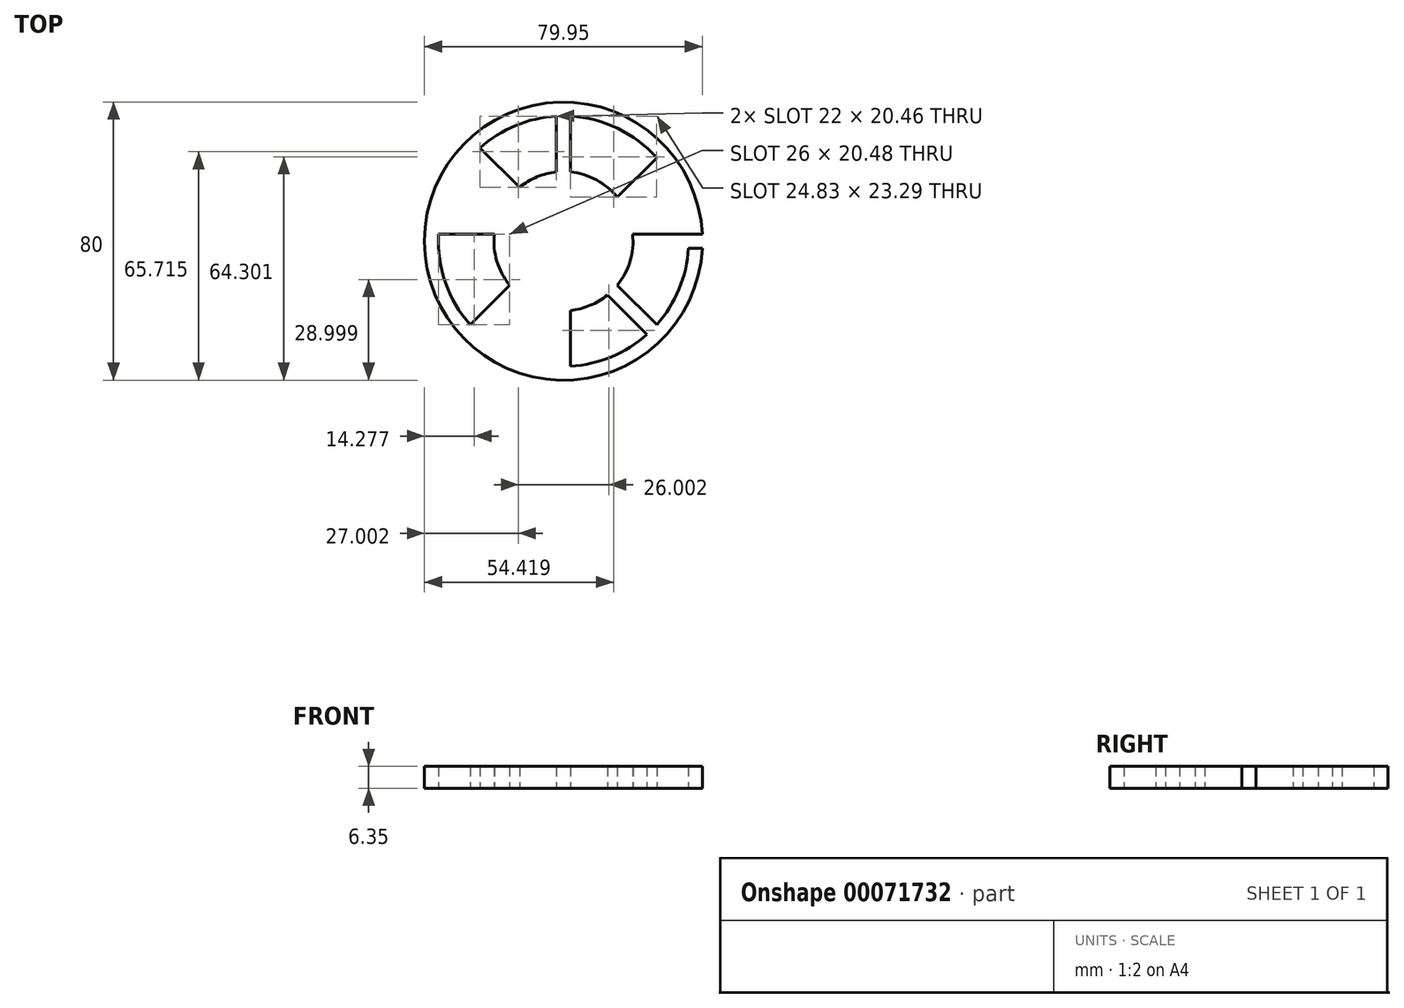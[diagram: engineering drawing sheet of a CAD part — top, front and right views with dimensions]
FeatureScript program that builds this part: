
annotation { "Feature Type Name" : "Feature", "Feature Type Description" : "" }
export const myFeature = defineFeature(function(context is Context, id is Id, definition is map)
    precondition{}
    {
        {
            var Q0;
            Q0=qCreatedBy(makeId("Top.planeOp"),FACE);
            var sketch = newSketch(context, id + "F0", { "sketchPlane" : qUnion([Q0])});
            skCircle(sketch, "E0", {"center": v(0.08, 0) * mm, "radius": 40 * mm});
            skCircle(sketch, "E1", {"center": v(0.08, 0) * mm, "radius": 36 * mm});
            skLineSegment(sketch, "E2.bottom", {"start": v(-1.92, 40) * mm, "end": v(2.08, 40) * mm});
            skLineSegment(sketch, "E2.top", {"start": v(-1.92, -40) * mm, "end": v(2.08, -40) * mm});
            skLineSegment(sketch, "E2.left", {"start": v(-1.92, 40) * mm, "end": v(-1.92, -40) * mm});
            skLineSegment(sketch, "E2.right", {"start": v(2.08, 40) * mm, "end": v(2.08, -40) * mm});
            skLineSegment(sketch, "E3", {"start": v(2.08, 0) * mm, "end": v(-1.92, 0) * mm, "construction": true});
            skPoint(sketch, "E3.endSnap0", {"position": v(-1.92, 0) * mm});
            skLineSegment(sketch, "E4.bottom", {"start": v(-39.92, -2) * mm, "end": v(40.08, -2) * mm});
            skLineSegment(sketch, "E4.top", {"start": v(-39.92, 2) * mm, "end": v(40.08, 2) * mm});
            skLineSegment(sketch, "E4.left", {"start": v(-39.92, 2) * mm, "end": v(-39.92, -2) * mm});
            skLineSegment(sketch, "E4.right", {"start": v(40.08, 2) * mm, "end": v(40.08, -2) * mm});
            skLineSegment(sketch, "E5", {"start": v(0.08, 2) * mm, "end": v(0.08, -2) * mm, "construction": true});
            skLineSegment(sketch, "E6.bottom", {"start": v(-26.79, -29.7) * mm, "end": v(29.78, 26.87) * mm});
            skLineSegment(sketch, "E6.top", {"start": v(-29.62, -26.87) * mm, "end": v(26.95, 29.7) * mm});
            skLineSegment(sketch, "E6.left", {"start": v(-29.62, -26.87) * mm, "end": v(-26.79, -29.7) * mm});
            skLineSegment(sketch, "E6.right", {"start": v(26.95, 29.7) * mm, "end": v(29.78, 26.87) * mm});
            skLineSegment(sketch, "E7", {"start": v(-1.33, 1.41) * mm, "end": v(1.5, -1.41) * mm, "construction": true});
            skLineSegment(sketch, "E8.bottom", {"start": v(-29.62, 26.87) * mm, "end": v(-26.79, 29.7) * mm});
            skLineSegment(sketch, "E8.top", {"start": v(26.95, -29.7) * mm, "end": v(29.78, -26.87) * mm});
            skLineSegment(sketch, "E8.left", {"start": v(-29.62, 26.87) * mm, "end": v(26.95, -29.7) * mm});
            skLineSegment(sketch, "E8.right", {"start": v(-26.79, 29.7) * mm, "end": v(29.78, -26.87) * mm});
            skLineSegment(sketch, "E9", {"start": v(-1.33, -1.41) * mm, "end": v(1.5, 1.41) * mm, "construction": true});
            skCircle(sketch, "E10", {"center": v(0.08, 0) * mm, "radius": 20 * mm});
            skSolve(sketch);
        }
        {
            var Q0;
            {var subQ0=sQuery(id+"F0.wireOp",EDGE,"E6.top");var subQ1=sQuery(id+"F0.wireOp",EDGE,"E0");var subQ2=makeQuery(id+"F0.imprint","INTERSECT",VERTEX,{"disambiguationData":[OD(0.0)],"derivedFrom":[subQ1,subQ0]});Q0=makeQuery(id+"F0.imprint","IMPRINT",FACE,{"disambiguationData":[TD([[makeQuery(id+"F0.imprint","IMPRINT",EDGE,{"disambiguationData":[TD([[subQ2,-1.0]])],"derivedFrom":subQ1}),1.0]])]});}
            var Q1;
            {var subQ1=sQuery(id+"F0.wireOp",EDGE,"E0");var subQ5=sQuery(id+"F0.wireOp",EDGE,"E2.right");var subQ7=makeQuery(id+"F0.imprint","INTERSECT",VERTEX,{"disambiguationData":[OD(0.0)],"derivedFrom":[subQ1,subQ5]});Q1=makeQuery(id+"F0.imprint","IMPRINT",FACE,{"disambiguationData":[TD([[makeQuery(id+"F0.imprint","IMPRINT",EDGE,{"disambiguationData":[TD([[subQ7,-1.0]])],"derivedFrom":subQ1}),1.0]])]});}
            var Q2;
            {var subQ0=sQuery(id+"F0.wireOp",EDGE,"E2.left");var subQ1=sQuery(id+"F0.wireOp",EDGE,"E0");var subQ2=makeQuery(id+"F0.imprint","INTERSECT",VERTEX,{"disambiguationData":[OD(0.0)],"derivedFrom":[subQ1,subQ0]});Q2=makeQuery(id+"F0.imprint","IMPRINT",FACE,{"disambiguationData":[TD([[makeQuery(id+"F0.imprint","IMPRINT",EDGE,{"disambiguationData":[TD([[subQ2,-1.0]])],"derivedFrom":subQ1}),1.0]])]});}
            var Q3;
            {var subQ1=sQuery(id+"F0.wireOp",EDGE,"E0");var subQ5=sQuery(id+"F0.wireOp",EDGE,"E8.right");var subQ6=makeQuery(id+"F0.imprint","INTERSECT",VERTEX,{"disambiguationData":[OD(0.0)],"derivedFrom":[subQ1,subQ5]});Q3=makeQuery(id+"F0.imprint","IMPRINT",FACE,{"disambiguationData":[TD([[makeQuery(id+"F0.imprint","IMPRINT",EDGE,{"disambiguationData":[TD([[subQ6,-1.0]])],"derivedFrom":subQ1}),1.0]])]});}
            var Q4;
            {var subQ0=sQuery(id+"F0.wireOp",EDGE,"E8.left");var subQ1=sQuery(id+"F0.wireOp",EDGE,"E0");var subQ2=makeQuery(id+"F0.imprint","INTERSECT",VERTEX,{"disambiguationData":[OD(0.0)],"derivedFrom":[subQ1,subQ0]});Q4=makeQuery(id+"F0.imprint","IMPRINT",FACE,{"disambiguationData":[TD([[makeQuery(id+"F0.imprint","IMPRINT",EDGE,{"disambiguationData":[TD([[subQ2,-1.0]])],"derivedFrom":subQ1}),1.0]])]});}
            var Q5;
            {var subQ1=sQuery(id+"F0.wireOp",EDGE,"E0");var subQ5=sQuery(id+"F0.wireOp",EDGE,"E4.top");var subQ8=makeQuery(id+"F0.imprint","INTERSECT",VERTEX,{"disambiguationData":[OD(1.0)],"derivedFrom":[subQ1,subQ5]});Q5=makeQuery(id+"F0.imprint","IMPRINT",FACE,{"disambiguationData":[TD([[makeQuery(id+"F0.imprint","IMPRINT",EDGE,{"disambiguationData":[TD([[subQ8,-1.0]])],"derivedFrom":subQ1}),1.0]])]});}
            var Q6;
            {var subQ0=sQuery(id+"F0.wireOp",EDGE,"E4.bottom");var subQ1=sQuery(id+"F0.wireOp",EDGE,"E0");var subQ2=makeQuery(id+"F0.imprint","INTERSECT",VERTEX,{"disambiguationData":[OD(0.0)],"derivedFrom":[subQ1,subQ0]});Q6=makeQuery(id+"F0.imprint","IMPRINT",FACE,{"disambiguationData":[TD([[makeQuery(id+"F0.imprint","IMPRINT",EDGE,{"disambiguationData":[TD([[subQ2,-1.0]])],"derivedFrom":subQ1}),1.0]])]});}
            var Q7;
            {var subQ1=sQuery(id+"F0.wireOp",EDGE,"E0");var subQ5=sQuery(id+"F0.wireOp",EDGE,"E6.top");var subQ6=makeQuery(id+"F0.imprint","INTERSECT",VERTEX,{"disambiguationData":[OD(1.0)],"derivedFrom":[subQ1,subQ5]});Q7=makeQuery(id+"F0.imprint","IMPRINT",FACE,{"disambiguationData":[TD([[makeQuery(id+"F0.imprint","IMPRINT",EDGE,{"disambiguationData":[TD([[subQ6,-1.0]])],"derivedFrom":subQ1}),1.0]])]});}
            var Q8;
            {var subQ0=sQuery(id+"F0.wireOp",EDGE,"E6.bottom");var subQ1=sQuery(id+"F0.wireOp",EDGE,"E0");var subQ2=makeQuery(id+"F0.imprint","INTERSECT",VERTEX,{"disambiguationData":[OD(1.0)],"derivedFrom":[subQ1,subQ0]});Q8=makeQuery(id+"F0.imprint","IMPRINT",FACE,{"disambiguationData":[TD([[makeQuery(id+"F0.imprint","IMPRINT",EDGE,{"disambiguationData":[TD([[subQ2,-1.0]])],"derivedFrom":subQ1}),1.0]])]});}
            var Q9;
            {var subQ0=sQuery(id+"F0.wireOp",EDGE,"E2.left");var subQ5=sQuery(id+"F0.wireOp",EDGE,"E0");var subQ6=makeQuery(id+"F0.imprint","INTERSECT",VERTEX,{"disambiguationData":[OD(1.0)],"derivedFrom":[subQ5,subQ0]});Q9=makeQuery(id+"F0.imprint","IMPRINT",FACE,{"disambiguationData":[TD([[makeQuery(id+"F0.imprint","IMPRINT",EDGE,{"disambiguationData":[TD([[subQ6,-1.0]])],"derivedFrom":subQ5}),1.0]])]});}
            var Q10;
            {var subQ0=sQuery(id+"F0.wireOp",EDGE,"E2.right");var subQ1=sQuery(id+"F0.wireOp",EDGE,"E0");var subQ2=makeQuery(id+"F0.imprint","INTERSECT",VERTEX,{"disambiguationData":[OD(1.0)],"derivedFrom":[subQ1,subQ0]});Q10=makeQuery(id+"F0.imprint","IMPRINT",FACE,{"disambiguationData":[TD([[makeQuery(id+"F0.imprint","IMPRINT",EDGE,{"disambiguationData":[TD([[subQ2,-1.0]])],"derivedFrom":subQ1}),1.0]])]});}
            var Q11;
            {var subQ0=sQuery(id+"F0.wireOp",EDGE,"E8.left");var subQ1=sQuery(id+"F0.wireOp",EDGE,"E0");var subQ2=makeQuery(id+"F0.imprint","INTERSECT",VERTEX,{"disambiguationData":[OD(1.0)],"derivedFrom":[subQ1,subQ0]});Q11=makeQuery(id+"F0.imprint","IMPRINT",FACE,{"disambiguationData":[TD([[makeQuery(id+"F0.imprint","IMPRINT",EDGE,{"disambiguationData":[TD([[subQ2,-1.0]])],"derivedFrom":subQ1}),1.0]])]});}
            var Q12;
            {var subQ0=sQuery(id+"F0.wireOp",EDGE,"E8.right");var subQ1=sQuery(id+"F0.wireOp",EDGE,"E0");var subQ2=makeQuery(id+"F0.imprint","INTERSECT",VERTEX,{"disambiguationData":[OD(1.0)],"derivedFrom":[subQ1,subQ0]});Q12=makeQuery(id+"F0.imprint","IMPRINT",FACE,{"disambiguationData":[TD([[makeQuery(id+"F0.imprint","IMPRINT",EDGE,{"disambiguationData":[TD([[subQ2,-1.0]])],"derivedFrom":subQ1}),1.0]])]});}
            var Q13;
            {var subQ1=sQuery(id+"F0.wireOp",EDGE,"E0");var subQ5=sQuery(id+"F0.wireOp",EDGE,"E4.top");var subQ7=makeQuery(id+"F0.imprint","INTERSECT",VERTEX,{"disambiguationData":[OD(0.0)],"derivedFrom":[subQ1,subQ5]});Q13=makeQuery(id+"F0.imprint","IMPRINT",FACE,{"disambiguationData":[TD([[makeQuery(id+"F0.imprint","IMPRINT",EDGE,{"disambiguationData":[TD([[subQ7,1.0]])],"derivedFrom":subQ1}),1.0]])]});}
            var Q14;
            {var subQ0=sQuery(id+"F0.wireOp",EDGE,"E4.top");var subQ1=sQuery(id+"F0.wireOp",EDGE,"E0");var subQ2=makeQuery(id+"F0.imprint","INTERSECT",VERTEX,{"disambiguationData":[OD(0.0)],"derivedFrom":[subQ1,subQ0]});Q14=makeQuery(id+"F0.imprint","IMPRINT",FACE,{"disambiguationData":[TD([[makeQuery(id+"F0.imprint","IMPRINT",EDGE,{"disambiguationData":[TD([[subQ2,-1.0]])],"derivedFrom":subQ1}),1.0]])]});}
            var Q15;
            {var subQ0=sQuery(id+"F0.wireOp",EDGE,"E6.bottom");var subQ1=sQuery(id+"F0.wireOp",EDGE,"E0");var subQ2=makeQuery(id+"F0.imprint","INTERSECT",VERTEX,{"disambiguationData":[OD(0.0)],"derivedFrom":[subQ1,subQ0]});Q15=makeQuery(id+"F0.imprint","IMPRINT",FACE,{"disambiguationData":[TD([[makeQuery(id+"F0.imprint","IMPRINT",EDGE,{"disambiguationData":[TD([[subQ2,-1.0]])],"derivedFrom":subQ1}),1.0]])]});}
            var Q16;
            {var subQ0=sQuery(id+"F0.wireOp",EDGE,"E6.bottom");var subQ1=sQuery(id+"F0.wireOp",EDGE,"E1");var subQ2=makeQuery(id+"F0.imprint","INTERSECT",VERTEX,{"disambiguationData":[OD(0.0)],"derivedFrom":[subQ1,subQ0]});Q16=makeQuery(id+"F0.imprint","IMPRINT",FACE,{"disambiguationData":[TD([[makeQuery(id+"F0.imprint","IMPRINT",EDGE,{"disambiguationData":[TD([[subQ2,-1.0]])],"derivedFrom":subQ1}),1.0]])]});}
            var Q17;
            {var subQ0=sQuery(id+"F0.wireOp",EDGE,"E4.top");var subQ1=sQuery(id+"F0.wireOp",EDGE,"E1");var subQ2=makeQuery(id+"F0.imprint","INTERSECT",VERTEX,{"disambiguationData":[OD(0.0)],"derivedFrom":[subQ1,subQ0]});Q17=makeQuery(id+"F0.imprint","IMPRINT",FACE,{"disambiguationData":[TD([[makeQuery(id+"F0.imprint","IMPRINT",EDGE,{"disambiguationData":[TD([[subQ2,1.0]])],"derivedFrom":subQ1}),1.0]])]});}
            var Q18;
            {var subQ0=sQuery(id+"F0.wireOp",EDGE,"E8.left");var subQ1=sQuery(id+"F0.wireOp",EDGE,"E1");var subQ2=makeQuery(id+"F0.imprint","INTERSECT",VERTEX,{"disambiguationData":[OD(1.0)],"derivedFrom":[subQ1,subQ0]});Q18=makeQuery(id+"F0.imprint","IMPRINT",FACE,{"disambiguationData":[TD([[makeQuery(id+"F0.imprint","IMPRINT",EDGE,{"disambiguationData":[TD([[subQ2,-1.0]])],"derivedFrom":subQ1}),1.0]])]});}
            var Q19;
            {var subQ0=sQuery(id+"F0.wireOp",EDGE,"E2.left");var subQ1=sQuery(id+"F0.wireOp",EDGE,"E1");var subQ2=makeQuery(id+"F0.imprint","INTERSECT",VERTEX,{"disambiguationData":[OD(1.0)],"derivedFrom":[subQ1,subQ0]});Q19=makeQuery(id+"F0.imprint","IMPRINT",FACE,{"disambiguationData":[TD([[makeQuery(id+"F0.imprint","IMPRINT",EDGE,{"disambiguationData":[TD([[subQ2,-1.0]])],"derivedFrom":subQ1}),1.0]])]});}
            var Q20;
            {var subQ0=sQuery(id+"F0.wireOp",EDGE,"E6.top");var subQ1=sQuery(id+"F0.wireOp",EDGE,"E1");var subQ2=makeQuery(id+"F0.imprint","INTERSECT",VERTEX,{"disambiguationData":[OD(1.0)],"derivedFrom":[subQ1,subQ0]});Q20=makeQuery(id+"F0.imprint","IMPRINT",FACE,{"disambiguationData":[TD([[makeQuery(id+"F0.imprint","IMPRINT",EDGE,{"disambiguationData":[TD([[subQ2,-1.0]])],"derivedFrom":subQ1}),1.0]])]});}
            var Q21;
            {var subQ0=sQuery(id+"F0.wireOp",EDGE,"E4.top");var subQ1=sQuery(id+"F0.wireOp",EDGE,"E1");var subQ2=makeQuery(id+"F0.imprint","INTERSECT",VERTEX,{"disambiguationData":[OD(1.0)],"derivedFrom":[subQ1,subQ0]});Q21=makeQuery(id+"F0.imprint","IMPRINT",FACE,{"disambiguationData":[TD([[makeQuery(id+"F0.imprint","IMPRINT",EDGE,{"disambiguationData":[TD([[subQ2,-1.0]])],"derivedFrom":subQ1}),1.0]])]});}
            var Q22;
            {var subQ0=sQuery(id+"F0.wireOp",EDGE,"E8.right");var subQ1=sQuery(id+"F0.wireOp",EDGE,"E1");var subQ2=makeQuery(id+"F0.imprint","INTERSECT",VERTEX,{"disambiguationData":[OD(0.0)],"derivedFrom":[subQ1,subQ0]});Q22=makeQuery(id+"F0.imprint","IMPRINT",FACE,{"disambiguationData":[TD([[makeQuery(id+"F0.imprint","IMPRINT",EDGE,{"disambiguationData":[TD([[subQ2,-1.0]])],"derivedFrom":subQ1}),1.0]])]});}
            var Q23;
            {var subQ0=sQuery(id+"F0.wireOp",EDGE,"E2.right");var subQ1=sQuery(id+"F0.wireOp",EDGE,"E1");var subQ2=makeQuery(id+"F0.imprint","INTERSECT",VERTEX,{"disambiguationData":[OD(0.0)],"derivedFrom":[subQ1,subQ0]});Q23=makeQuery(id+"F0.imprint","IMPRINT",FACE,{"disambiguationData":[TD([[makeQuery(id+"F0.imprint","IMPRINT",EDGE,{"disambiguationData":[TD([[subQ2,-1.0]])],"derivedFrom":subQ1}),1.0]])]});}
            var Q24;
            {var subQ1=sQuery(id+"F0.wireOp",EDGE,"E2.left");var subQ5=sQuery(id+"F0.wireOp",EDGE,"E10");var subQ9=makeQuery(id+"F0.imprint","INTERSECT",VERTEX,{"disambiguationData":[OD(0.0)],"derivedFrom":[subQ1,subQ5]});Q24=makeQuery(id+"F0.imprint","IMPRINT",FACE,{"disambiguationData":[TD([[makeQuery(id+"F0.imprint","IMPRINT",EDGE,{"disambiguationData":[TD([[subQ9,-1.0]])],"derivedFrom":subQ1}),1.0]])]});}
            var Q25;
            {var subQ0=sQuery(id+"F0.wireOp",EDGE,"E10");var subQ1=sQuery(id+"F0.wireOp",EDGE,"E2.right");var subQ2=makeQuery(id+"F0.imprint","INTERSECT",VERTEX,{"disambiguationData":[OD(0.0)],"derivedFrom":[subQ1,subQ0]});Q25=makeQuery(id+"F0.imprint","IMPRINT",FACE,{"disambiguationData":[TD([[makeQuery(id+"F0.imprint","IMPRINT",EDGE,{"disambiguationData":[TD([[subQ2,-1.0]])],"derivedFrom":subQ1}),1.0]])]});}
            var Q26;
            {var subQ0=sQuery(id+"F0.wireOp",EDGE,"E6.top");var subQ1=sQuery(id+"F0.wireOp",EDGE,"E2.right");var subQ2=makeQuery(id+"F0.imprint","INTERSECT",VERTEX,{"derivedFrom":[subQ1,subQ0]});Q26=makeQuery(id+"F0.imprint","IMPRINT",FACE,{"disambiguationData":[TD([[makeQuery(id+"F0.imprint","IMPRINT",EDGE,{"disambiguationData":[TD([[subQ2,-1.0]])],"derivedFrom":subQ1}),1.0]])]});}
            var Q27;
            {var subQ0=sQuery(id+"F0.wireOp",EDGE,"E8.right");var subQ1=sQuery(id+"F0.wireOp",EDGE,"E4.bottom");var subQ2=makeQuery(id+"F0.imprint","INTERSECT",VERTEX,{"derivedFrom":[subQ1,subQ0]});Q27=makeQuery(id+"F0.imprint","IMPRINT",FACE,{"disambiguationData":[TD([[makeQuery(id+"F0.imprint","IMPRINT",EDGE,{"disambiguationData":[TD([[subQ2,-1.0]])],"derivedFrom":subQ1}),1.0]])]});}
            var Q28;
            {var subQ0=sQuery(id+"F0.wireOp",EDGE,"E6.bottom");var subQ1=sQuery(id+"F0.wireOp",EDGE,"E4.top");var subQ2=makeQuery(id+"F0.imprint","INTERSECT",VERTEX,{"derivedFrom":[subQ1,subQ0]});Q28=makeQuery(id+"F0.imprint","IMPRINT",FACE,{"disambiguationData":[TD([[makeQuery(id+"F0.imprint","IMPRINT",EDGE,{"disambiguationData":[TD([[subQ2,-1.0]])],"derivedFrom":subQ1}),1.0]])]});}
            var Q29;
            {var subQ0=sQuery(id+"F0.wireOp",EDGE,"E8.right");var subQ1=sQuery(id+"F0.wireOp",EDGE,"E4.bottom");var subQ2=makeQuery(id+"F0.imprint","INTERSECT",VERTEX,{"derivedFrom":[subQ1,subQ0]});Q29=makeQuery(id+"F0.imprint","IMPRINT",FACE,{"disambiguationData":[TD([[makeQuery(id+"F0.imprint","IMPRINT",EDGE,{"disambiguationData":[TD([[subQ2,-1.0]])],"derivedFrom":subQ1}),-1.0]])]});}
            var Q30;
            {var subQ1=sQuery(id+"F0.wireOp",EDGE,"E4.bottom");var subQ6=sQuery(id+"F0.wireOp",EDGE,"E2.right");var subQ9=makeQuery(id+"F0.imprint","INTERSECT",VERTEX,{"derivedFrom":[subQ6,subQ1]});Q30=makeQuery(id+"F0.imprint","IMPRINT",FACE,{"disambiguationData":[TD([[makeQuery(id+"F0.imprint","IMPRINT",EDGE,{"disambiguationData":[TD([[subQ9,-1.0]])],"derivedFrom":subQ6}),1.0]])]});}
            var Q31;
            {var subQ0=sQuery(id+"F0.wireOp",EDGE,"E8.left");var subQ1=sQuery(id+"F0.wireOp",EDGE,"E2.right");var subQ2=makeQuery(id+"F0.imprint","INTERSECT",VERTEX,{"derivedFrom":[subQ1,subQ0]});Q31=makeQuery(id+"F0.imprint","IMPRINT",FACE,{"disambiguationData":[TD([[makeQuery(id+"F0.imprint","IMPRINT",EDGE,{"disambiguationData":[TD([[subQ2,-1.0]])],"derivedFrom":subQ1}),1.0]])]});}
            var Q32;
            {var subQ3=sQuery(id+"F0.wireOp",EDGE,"E6.bottom");var subQ5=sQuery(id+"F0.wireOp",EDGE,"E2.left");var subQ6=makeQuery(id+"F0.imprint","INTERSECT",VERTEX,{"derivedFrom":[subQ5,subQ3]});Q32=makeQuery(id+"F0.imprint","IMPRINT",FACE,{"disambiguationData":[TD([[makeQuery(id+"F0.imprint","IMPRINT",EDGE,{"disambiguationData":[TD([[subQ6,-1.0]])],"derivedFrom":subQ5}),1.0]])]});}
            var Q33;
            {var subQ0=sQuery(id+"F0.wireOp",EDGE,"E6.bottom");var subQ1=sQuery(id+"F0.wireOp",EDGE,"E2.left");var subQ2=makeQuery(id+"F0.imprint","INTERSECT",VERTEX,{"derivedFrom":[subQ1,subQ0]});Q33=makeQuery(id+"F0.imprint","IMPRINT",FACE,{"disambiguationData":[TD([[makeQuery(id+"F0.imprint","IMPRINT",EDGE,{"disambiguationData":[TD([[subQ2,-1.0]])],"derivedFrom":subQ1}),-1.0]])]});}
            var Q34;
            {var subQ1=sQuery(id+"F0.wireOp",EDGE,"E4.bottom");var subQ5=sQuery(id+"F0.wireOp",EDGE,"E2.left");var subQ6=makeQuery(id+"F0.imprint","INTERSECT",VERTEX,{"derivedFrom":[subQ5,subQ1]});Q34=makeQuery(id+"F0.imprint","IMPRINT",FACE,{"disambiguationData":[TD([[makeQuery(id+"F0.imprint","IMPRINT",EDGE,{"disambiguationData":[TD([[subQ6,-1.0]])],"derivedFrom":subQ5}),-1.0]])]});}
            var Q35;
            {var subQ0=sQuery(id+"F0.wireOp",EDGE,"E10");var subQ1=sQuery(id+"F0.wireOp",EDGE,"E4.bottom");var subQ2=makeQuery(id+"F0.imprint","INTERSECT",VERTEX,{"disambiguationData":[OD(0.0)],"derivedFrom":[subQ1,subQ0]});Q35=makeQuery(id+"F0.imprint","IMPRINT",FACE,{"disambiguationData":[TD([[makeQuery(id+"F0.imprint","IMPRINT",EDGE,{"disambiguationData":[TD([[subQ2,-1.0]])],"derivedFrom":subQ1}),-1.0]])]});}
            var Q36;
            {var subQ5=sQuery(id+"F0.wireOp",EDGE,"E4.bottom");var subQ7=sQuery(id+"F0.wireOp",EDGE,"E10");var subQ9=makeQuery(id+"F0.imprint","INTERSECT",VERTEX,{"disambiguationData":[OD(0.0)],"derivedFrom":[subQ5,subQ7]});Q36=makeQuery(id+"F0.imprint","IMPRINT",FACE,{"disambiguationData":[TD([[makeQuery(id+"F0.imprint","IMPRINT",EDGE,{"disambiguationData":[TD([[subQ9,-1.0]])],"derivedFrom":subQ5}),1.0]])]});}
            var Q37;
            {var subQ0=sQuery(id+"F0.wireOp",EDGE,"E10");var subQ1=sQuery(id+"F0.wireOp",EDGE,"E4.top");var subQ2=makeQuery(id+"F0.imprint","INTERSECT",VERTEX,{"disambiguationData":[OD(0.0)],"derivedFrom":[subQ1,subQ0]});Q37=makeQuery(id+"F0.imprint","IMPRINT",FACE,{"disambiguationData":[TD([[makeQuery(id+"F0.imprint","IMPRINT",EDGE,{"disambiguationData":[TD([[subQ2,-1.0]])],"derivedFrom":subQ1}),1.0]])]});}
            var Q38;
            {var subQ5=sQuery(id+"F0.wireOp",EDGE,"E8.right");var subQ6=sQuery(id+"F0.wireOp",EDGE,"E2.left");var subQ7=makeQuery(id+"F0.imprint","INTERSECT",VERTEX,{"derivedFrom":[subQ6,subQ5]});Q38=makeQuery(id+"F0.imprint","IMPRINT",FACE,{"disambiguationData":[TD([[makeQuery(id+"F0.imprint","IMPRINT",EDGE,{"disambiguationData":[TD([[subQ7,-1.0]])],"derivedFrom":subQ6}),-1.0]])]});}
            var Q39;
            {var subQ0=sQuery(id+"F0.wireOp",EDGE,"E10");var subQ1=sQuery(id+"F0.wireOp",EDGE,"E2.left");var subQ2=makeQuery(id+"F0.imprint","INTERSECT",VERTEX,{"disambiguationData":[OD(0.0)],"derivedFrom":[subQ1,subQ0]});Q39=makeQuery(id+"F0.imprint","IMPRINT",FACE,{"disambiguationData":[TD([[makeQuery(id+"F0.imprint","IMPRINT",EDGE,{"disambiguationData":[TD([[subQ2,-1.0]])],"derivedFrom":subQ1}),-1.0]])]});}
            var Q40;
            {var subQ0=sQuery(id+"F0.wireOp",EDGE,"E4.top");var subQ1=sQuery(id+"F0.wireOp",EDGE,"E2.right");var subQ2=makeQuery(id+"F0.imprint","INTERSECT",VERTEX,{"derivedFrom":[subQ1,subQ0]});Q40=makeQuery(id+"F0.imprint","IMPRINT",FACE,{"disambiguationData":[TD([[makeQuery(id+"F0.imprint","IMPRINT",EDGE,{"disambiguationData":[TD([[subQ2,-1.0]])],"derivedFrom":subQ1}),1.0]])]});}
            var Q41;
            {var subQ0=sQuery(id+"F0.wireOp",EDGE,"E6.bottom");var subQ1=sQuery(id+"F0.wireOp",EDGE,"E2.right");var subQ2=makeQuery(id+"F0.imprint","INTERSECT",VERTEX,{"derivedFrom":[subQ1,subQ0]});Q41=makeQuery(id+"F0.imprint","IMPRINT",FACE,{"disambiguationData":[TD([[makeQuery(id+"F0.imprint","IMPRINT",EDGE,{"disambiguationData":[TD([[subQ2,-1.0]])],"derivedFrom":subQ1}),1.0]])]});}
            var Q42;
            {var subQ0=sQuery(id+"F0.wireOp",EDGE,"E4.bottom");var subQ1=sQuery(id+"F0.wireOp",EDGE,"E2.right");var subQ2=makeQuery(id+"F0.imprint","INTERSECT",VERTEX,{"derivedFrom":[subQ1,subQ0]});Q42=makeQuery(id+"F0.imprint","IMPRINT",FACE,{"disambiguationData":[TD([[makeQuery(id+"F0.imprint","IMPRINT",EDGE,{"disambiguationData":[TD([[subQ2,-1.0]])],"derivedFrom":subQ1}),-1.0]])]});}
            var Q43;
            {var subQ0=sQuery(id+"F0.wireOp",EDGE,"E4.bottom");var subQ1=sQuery(id+"F0.wireOp",EDGE,"E2.left");var subQ2=makeQuery(id+"F0.imprint","INTERSECT",VERTEX,{"derivedFrom":[subQ1,subQ0]});Q43=makeQuery(id+"F0.imprint","IMPRINT",FACE,{"disambiguationData":[TD([[makeQuery(id+"F0.imprint","IMPRINT",EDGE,{"disambiguationData":[TD([[subQ2,-1.0]])],"derivedFrom":subQ1}),1.0]])]});}
            var Q44;
            {var subQ0=sQuery(id+"F0.wireOp",EDGE,"E4.top");var subQ1=sQuery(id+"F0.wireOp",EDGE,"E2.left");var subQ2=makeQuery(id+"F0.imprint","INTERSECT",VERTEX,{"derivedFrom":[subQ1,subQ0]});Q44=makeQuery(id+"F0.imprint","IMPRINT",FACE,{"disambiguationData":[TD([[makeQuery(id+"F0.imprint","IMPRINT",EDGE,{"disambiguationData":[TD([[subQ2,-1.0]])],"derivedFrom":subQ1}),-1.0]])]});}
            var Q45;
            {var subQ0=sQuery(id+"F0.wireOp",EDGE,"E6.top");var subQ1=sQuery(id+"F0.wireOp",EDGE,"E2.right");var subQ2=makeQuery(id+"F0.imprint","INTERSECT",VERTEX,{"derivedFrom":[subQ1,subQ0]});Q45=makeQuery(id+"F0.imprint","IMPRINT",FACE,{"disambiguationData":[TD([[makeQuery(id+"F0.imprint","IMPRINT",EDGE,{"disambiguationData":[TD([[subQ2,-1.0]])],"derivedFrom":subQ1}),-1.0]])]});}
            var Q46;
            {var subQ0=sQuery(id+"F0.wireOp",EDGE,"E8.right");var subQ1=sQuery(id+"F0.wireOp",EDGE,"E2.right");var subQ2=makeQuery(id+"F0.imprint","INTERSECT",VERTEX,{"derivedFrom":[subQ1,subQ0]});Q46=makeQuery(id+"F0.imprint","IMPRINT",FACE,{"disambiguationData":[TD([[makeQuery(id+"F0.imprint","IMPRINT",EDGE,{"disambiguationData":[TD([[subQ2,-1.0]])],"derivedFrom":subQ1}),1.0]])]});}
            var Q47;
            {var subQ0=sQuery(id+"F0.wireOp",EDGE,"E6.bottom");var subQ1=sQuery(id+"F0.wireOp",EDGE,"E2.right");var subQ2=makeQuery(id+"F0.imprint","INTERSECT",VERTEX,{"derivedFrom":[subQ1,subQ0]});Q47=makeQuery(id+"F0.imprint","IMPRINT",FACE,{"disambiguationData":[TD([[makeQuery(id+"F0.imprint","IMPRINT",EDGE,{"disambiguationData":[TD([[subQ2,-1.0]])],"derivedFrom":subQ1}),-1.0]])]});}
            var Q48;
            {var subQ0=sQuery(id+"F0.wireOp",EDGE,"E8.left");var subQ1=sQuery(id+"F0.wireOp",EDGE,"E4.bottom");var subQ2=makeQuery(id+"F0.imprint","INTERSECT",VERTEX,{"derivedFrom":[subQ1,subQ0]});Q48=makeQuery(id+"F0.imprint","IMPRINT",FACE,{"disambiguationData":[TD([[makeQuery(id+"F0.imprint","IMPRINT",EDGE,{"disambiguationData":[TD([[subQ2,-1.0]])],"derivedFrom":subQ1}),-1.0]])]});}
            var Q49;
            {var subQ0=sQuery(id+"F0.wireOp",EDGE,"E6.top");var subQ1=sQuery(id+"F0.wireOp",EDGE,"E2.left");var subQ2=makeQuery(id+"F0.imprint","INTERSECT",VERTEX,{"derivedFrom":[subQ1,subQ0]});Q49=makeQuery(id+"F0.imprint","IMPRINT",FACE,{"disambiguationData":[TD([[makeQuery(id+"F0.imprint","IMPRINT",EDGE,{"disambiguationData":[TD([[subQ2,-1.0]])],"derivedFrom":subQ1}),-1.0]])]});}
            var Q50;
            {var subQ0=sQuery(id+"F0.wireOp",EDGE,"E4.top");var subQ1=sQuery(id+"F0.wireOp",EDGE,"E2.left");var subQ2=makeQuery(id+"F0.imprint","INTERSECT",VERTEX,{"derivedFrom":[subQ1,subQ0]});Q50=makeQuery(id+"F0.imprint","IMPRINT",FACE,{"disambiguationData":[TD([[makeQuery(id+"F0.imprint","IMPRINT",EDGE,{"disambiguationData":[TD([[subQ2,-1.0]])],"derivedFrom":subQ1}),1.0]])]});}
            var Q51;
            {var subQ0=sQuery(id+"F0.wireOp",EDGE,"E8.right");var subQ1=sQuery(id+"F0.wireOp",EDGE,"E2.left");var subQ2=makeQuery(id+"F0.imprint","INTERSECT",VERTEX,{"derivedFrom":[subQ1,subQ0]});Q51=makeQuery(id+"F0.imprint","IMPRINT",FACE,{"disambiguationData":[TD([[makeQuery(id+"F0.imprint","IMPRINT",EDGE,{"disambiguationData":[TD([[subQ2,-1.0]])],"derivedFrom":subQ1}),1.0]])]});}
            var Q52;
            {var subQ0=sQuery(id+"F0.wireOp",EDGE,"E6.top");var subQ1=sQuery(id+"F0.wireOp",EDGE,"E4.top");var subQ2=makeQuery(id+"F0.imprint","INTERSECT",VERTEX,{"derivedFrom":[subQ1,subQ0]});Q52=makeQuery(id+"F0.imprint","IMPRINT",FACE,{"disambiguationData":[TD([[makeQuery(id+"F0.imprint","IMPRINT",EDGE,{"disambiguationData":[TD([[subQ2,-1.0]])],"derivedFrom":subQ1}),1.0]])]});}
            var Q53;
            {var subQ0=sQuery(id+"F0.wireOp",EDGE,"E8.left");var subQ1=sQuery(id+"F0.wireOp",EDGE,"E2.left");var subQ2=makeQuery(id+"F0.imprint","INTERSECT",VERTEX,{"derivedFrom":[subQ1,subQ0]});Q53=makeQuery(id+"F0.imprint","IMPRINT",FACE,{"disambiguationData":[TD([[makeQuery(id+"F0.imprint","IMPRINT",EDGE,{"disambiguationData":[TD([[subQ2,-1.0]])],"derivedFrom":subQ1}),-1.0]])]});}
            var Q54;
            {var subQ0=sQuery(id+"F0.wireOp",EDGE,"E6.top");var subQ13=sQuery(id+"F0.wireOp",EDGE,"E2.left");var subQ14=makeQuery(id+"F0.imprint","INTERSECT",VERTEX,{"derivedFrom":[subQ13,subQ0]});Q54=makeQuery(id+"F0.imprint","IMPRINT",FACE,{"disambiguationData":[TD([[makeQuery(id+"F0.imprint","IMPRINT",EDGE,{"disambiguationData":[TD([[subQ14,-1.0]])],"derivedFrom":subQ13}),1.0]])]});}
            var Q55;
            {var subQ0=sQuery(id+"F0.wireOp",EDGE,"E8.left");var subQ1=sQuery(id+"F0.wireOp",EDGE,"E2.left");var subQ2=makeQuery(id+"F0.imprint","INTERSECT",VERTEX,{"derivedFrom":[subQ1,subQ0]});Q55=makeQuery(id+"F0.imprint","IMPRINT",FACE,{"disambiguationData":[TD([[makeQuery(id+"F0.imprint","IMPRINT",EDGE,{"disambiguationData":[TD([[subQ2,-1.0]])],"derivedFrom":subQ1}),1.0]])]});}
            var Q56;
            {var subQ0=sQuery(id+"F0.wireOp",EDGE,"E4.top");var subQ1=sQuery(id+"F0.wireOp",EDGE,"E2.right");var subQ2=makeQuery(id+"F0.imprint","INTERSECT",VERTEX,{"derivedFrom":[subQ1,subQ0]});Q56=makeQuery(id+"F0.imprint","IMPRINT",FACE,{"disambiguationData":[TD([[makeQuery(id+"F0.imprint","IMPRINT",EDGE,{"disambiguationData":[TD([[subQ2,-1.0]])],"derivedFrom":subQ1}),-1.0]])]});}
            extrude(context, id + "F1", {"entities" : qUnion([Q0, Q1, Q2, Q3, Q4, Q5, Q6, Q7, Q8, Q9, Q10, Q11, Q12, Q13, Q14, Q15, Q16, Q17, Q18, Q19, Q20, Q21, Q22, Q23, Q24, Q25, Q26, Q27, Q28, Q29, Q30, Q31, Q32, Q33, Q34, Q35, Q36, Q37, Q38, Q39, Q40, Q41, Q42, Q43, Q44, Q45, Q46, Q47, Q48, Q49, Q50, Q51, Q52, Q53, Q54, Q55, Q56]), "depth" : 6.35 * mm});
        }
    });
